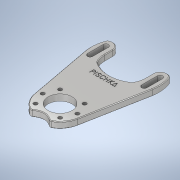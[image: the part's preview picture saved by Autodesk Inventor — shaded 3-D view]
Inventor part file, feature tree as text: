
AUTODESK INVENTOR PART (.ipt)
format: ipt  version: 2020.1 (Build 241239000, 239)  size: 884,224 bytes
history: native  units: mm
features: thread x6, emboss x2, fillet x2, extrude x1, chamfer x1, other x1, sketch x1
ambient origin geometry x8: Origin, YZ Plane, XZ Plane, XY Plane, X Axis, Y Axis, Z Axis, Center Point
bodies: Body1 (feature_tree)
feature tree (14):
  extrude  "Extrusion3"  Depth=19.0mm
  thread  "Thread1"  [1 undecoded]
  thread  "Thread2"  [1 undecoded]
  thread  "Thread4"  [1 undecoded]
  thread  "Thread5"  [1 undecoded]
  thread  "Thread6"  [1 undecoded]
  thread  "Thread7"  [1 undecoded]
  emboss  "Emboss1"
  emboss  "Emboss2"
  fillet  "Fillet3"  Radius=3.0mm
  fillet  "Fillet5"  Radius=3.0mm
  chamfer  "Chamfer3"  Angle=45.0deg  [1 undecoded]
  other  "Center Lines"
  sketch  "Sketch1"  dims[d0=51.5mm d1=19.0mm d3=3.5mm d4=3.5mm d5=7.0mm d9=3.5mm d11=32.0mm d15=4.1mm d24=3.0mm d25=3.0mm d27=45.0deg d29=3.0mm d30=3.0mm d40=5.0mm d41=0.0mm d44=10.0mm d45=0.0mm d46=10.0mm d47=0.0mm d50=15.0mm d51=52.0mm d53=27.0mm d54=10.0mm d55=0.0mm d56=10.0mm d57=0.0mm d58=10.0mm d59=0.0mm d60=10.0mm d61=0.0mm d65=0.5mm d66=0.0mm d73=0.5mm d74=0.0mm d75=80.75mm d76=8.0mm d78=0.0mm d81=6.25mm d82=12.5mm d85=5.0mm d86=4.0mm d91=0.5mm d94=2.0mm d95=0.5mm d96=2.0mm d97=45.0deg d98=15.0deg d99=24.0mm d101=43.0mm d104=2.0mm d105=27.5mm]
note: 7 required parameter values undecoded (feature->parameter linkage not recoverable at this tier; creation-order binding heuristic only, values carry confidence <= 0.55)
